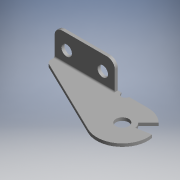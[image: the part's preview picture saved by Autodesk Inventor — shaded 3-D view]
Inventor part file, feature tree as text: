
AUTODESK INVENTOR PART (.ipt)
format: ipt  version: 2017.3 (Build 213256000, 256)  size: 162,816 bytes
history: native  units: mm (DEFAULTED — no unit token found)
features: other x28, extrude x6, sketch x6
ambient origin geometry x8: Origin, YZ Plane, XZ Plane, XY Plane, X Axis, Y Axis, Z Axis, Center Point
bodies: Solid1 (feature_tree)
feature tree (40):
  extrude  "Extrusion1"  Depth=188.0mm TaperAngle=0.0deg
  extrude  "Extrusion2"  Depth=4.0mm TaperAngle=0.0deg
  extrude  "Extrusion3"  Depth=20.0mm TaperAngle=0.0deg
  extrude  "Extrusion4"  [1 undecoded]
  extrude  "Extrusion5"  [1 undecoded]
  extrude  "Extrusion6"  [1 undecoded]
  other  "fix_end_l_XY"
  other  "fix_end_l_YZ"
  other  "fix_end_l_ZX"
  other  "fix_end_l_X"
  other  "fix_end_l_Y"
  other  "fix_end_l_Z"
  other  "fix_end_l_Center"
  other  "free_end_l_XY"
  other  "free_end_l_YZ"
  other  "free_end_l_ZX"
  other  "free_end_l_X"
  other  "free_end_l_Y"
  other  "free_end_l_Z"
  other  "free_end_l_Center"
  other  "l_to_r_XY"
  other  "l_to_r_YZ"
  other  "l_to_r_ZX"
  other  "l_to_r_X"
  other  "l_to_r_Y"
  other  "l_to_r_Z"
  other  "l_to_r_Center"
  other  "to_clip5_XY"
  other  "to_clip5_YZ"
  other  "to_clip5_ZX"
  other  "to_clip5_X"
  other  "to_clip5_Y"
  other  "to_clip5_Z"
  other  "to_clip5_Center"
  sketch  "Sketch_10"
  sketch  "Sketch_11"
  sketch  "Sketch_3"  dims[d8=4.0mm d9=0.0mm d10=20.0mm d11=0.0mm]
  sketch  "Sketch_1"  dims[d0=20.0mm d1=0.0mm d2=188.0mm d3=0.0mm]
  sketch  "Sketch_2"  dims[d4=34.0mm d5=0.0mm d6=4.0mm d7=0.0mm]
  sketch  "Sketch_7"  dims[d12=0.0mm d13=0.0mm]
note: 3 required parameter values undecoded (feature->parameter linkage not recoverable at this tier; creation-order binding heuristic only, values carry confidence <= 0.55)
